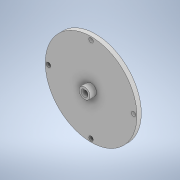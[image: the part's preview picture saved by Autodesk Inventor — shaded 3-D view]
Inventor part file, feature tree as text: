
AUTODESK INVENTOR PART (.ipt)
format: ipt  version: 2020 (Build 240168000, 168)  size: 143,872 bytes
history: native  units: in
note: dims shown in document units (in); Inventor stores cm internally (conversion verified against a paired STEP export)
features: extrude x5, sketch x4, pattern_circular x1
ambient origin geometry x8: Origin, YZ Plane, XZ Plane, XY Plane, X Axis, Y Axis, Z Axis, Center Point
bodies: Solid1 (feature_tree)
feature tree (10):
  sketch  "Sketch1"  dims[d0=16.5354in d4=0.7874in d5=0.0in]
  extrude  "Extrusion1"  Depth=0.7874in TaperAngle=0.0deg
  sketch  "Sketch3"  dims[d8=1.1811in d9=0.0in d10=0.7874in d11=0.0in]
  extrude  "Extrusion2"  Depth=1.9685in
  extrude  "Extrusion3"  Depth=0.7874in TaperAngle=0.0deg
  extrude  "Extrusion4"  Depth=0.7874in
  extrude  "Extrusion5"  Depth=0.7874in TaperAngle=0.0deg
  pattern_circular  "Circular Pattern1"  [2 undecoded]
  sketch  "Sketch2"  dims[d6=1.9685in d7=1.25in]
  sketch  "Sketch5"  dims[d12=14.1732in d13=0.7874in d17=0.7874in d18=0.0in d19=0.3937in d20=0.1969in d21=1.1811in d22=0.0in d23=7.6772in d24=1.5748in d25=360.0deg d2=0.0197in d3=0.0344in]
note: 2 required parameter values undecoded (feature->parameter linkage not recoverable at this tier; creation-order binding heuristic only, values carry confidence <= 0.55)
